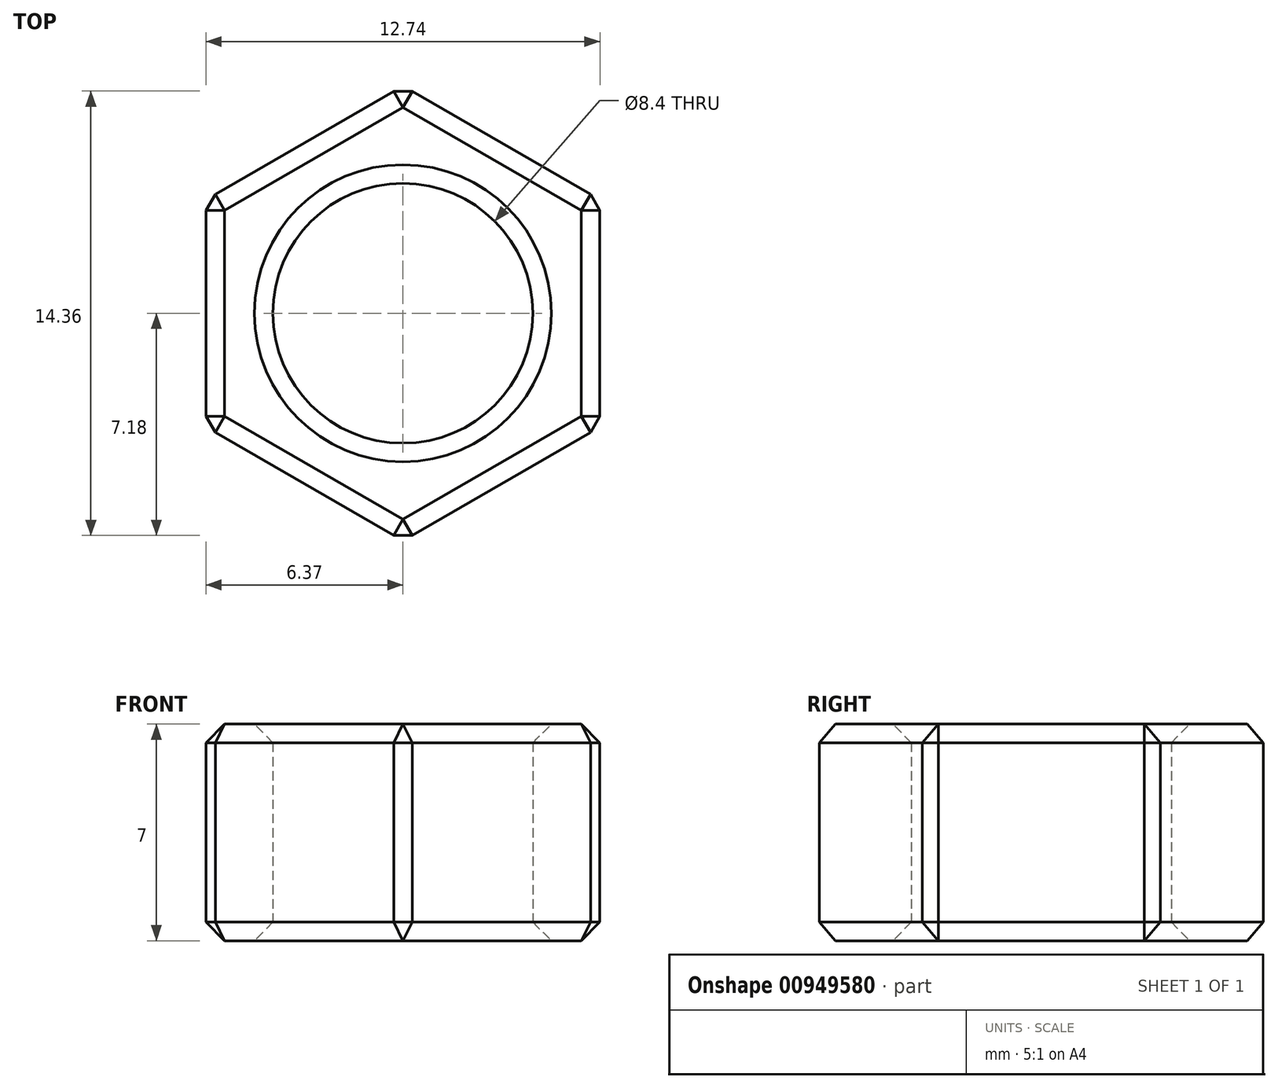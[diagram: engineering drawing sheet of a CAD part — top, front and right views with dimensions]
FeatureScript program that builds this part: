
annotation { "Feature Type Name" : "Feature", "Feature Type Description" : "" }
export const myFeature = defineFeature(function(context is Context, id is Id, definition is map)
    precondition{}
    {
        {
            var Q0;
            Q0=qCreatedBy(makeId("Top.planeOp"),FACE);
            var sketch = newSketch(context, id + "F0", { "sketchPlane" : qUnion([Q0])});
            skCircle(sketch, "E0.cCircle", {"center": v(0, 0) * mm, "radius": 7.35 * mm, "construction": true});
            skLineSegment(sketch, "E0.0", {"start": v(0, -7.35) * mm, "end": v(-6.37, -3.67) * mm});
            skLineSegment(sketch, "E0.1", {"start": v(-6.37, -3.68) * mm, "end": v(-6.37, 3.67) * mm});
            skLineSegment(sketch, "E0.2", {"start": v(-6.37, 3.67) * mm, "end": v(0, 7.35) * mm});
            skLineSegment(sketch, "E0.3", {"start": v(0, 7.35) * mm, "end": v(6.37, 3.68) * mm});
            skLineSegment(sketch, "E0.4", {"start": v(6.37, 3.68) * mm, "end": v(6.37, -3.67) * mm});
            skLineSegment(sketch, "E0.5", {"start": v(6.37, -3.67) * mm, "end": v(0, -7.35) * mm});
            skCircle(sketch, "E1", {"center": v(0, 0) * mm, "radius": 4.2 * mm});
            skSolve(sketch);
        }
        {
            var Q0;
            Q0=makeQuery(id+"F0.imprint","IMPRINT",FACE,{"disambiguationData":[TD([[makeQuery(id+"F0.imprint","IMPRINT",EDGE,{"derivedFrom":sQuery(id+"F0.wireOp",EDGE,"E0.0")}),-1.0]])]});
            extrude(context, id + "F1", {"entities" : qUnion([Q0]), "depth" : 7 * mm, "offsetDistance" : 25 * mm});
        }
        {
            var Q0;
            Q0=makeQuery(id+"F1.opExtrude","CAP_EDGE",EDGE,{"disambiguationData":[OSD([sQuery(id+"F0.wireOp",EDGE,"E0.4")])],"isStart":true});
            var Q1;
            Q1=makeQuery(id+"F1.opExtrude","CAP_EDGE",EDGE,{"disambiguationData":[OSD([sQuery(id+"F0.wireOp",EDGE,"E0.4")])],"isStart":false});
            var Q2;
            Q2=makeQuery(id+"F1.opExtrude","SWEPT_EDGE",EDGE,{"disambiguationData":[OSD([sQuery(id+"F0.wireOp",EDGE,"E0.0"),sQuery(id+"F0.wireOp",EDGE,"E0.5")])]});
            var Q3;
            Q3=makeQuery(id+"F1.opExtrude","SWEPT_EDGE",EDGE,{"disambiguationData":[OSD([sQuery(id+"F0.wireOp",EDGE,"E0.0"),sQuery(id+"F0.wireOp",EDGE,"E0.1")])]});
            var Q4;
            Q4=makeQuery(id+"F1.opExtrude","SWEPT_EDGE",EDGE,{"disambiguationData":[OSD([sQuery(id+"F0.wireOp",EDGE,"E0.3"),sQuery(id+"F0.wireOp",EDGE,"E0.4")])]});
            var Q5;
            Q5=makeQuery(id+"F1.opExtrude","SWEPT_EDGE",EDGE,{"disambiguationData":[OSD([sQuery(id+"F0.wireOp",EDGE,"E0.4"),sQuery(id+"F0.wireOp",EDGE,"E0.5")])]});
            var Q6;
            Q6=makeQuery(id+"F1.opExtrude","CAP_EDGE",EDGE,{"disambiguationData":[OSD([sQuery(id+"F0.wireOp",EDGE,"E0.1")])],"isStart":false});
            var Q7;
            Q7=makeQuery(id+"F1.opExtrude","CAP_EDGE",EDGE,{"disambiguationData":[OSD([sQuery(id+"F0.wireOp",EDGE,"E0.2")])],"isStart":false});
            var Q8;
            Q8=makeQuery(id+"F1.opExtrude","CAP_EDGE",EDGE,{"disambiguationData":[OSD([sQuery(id+"F0.wireOp",EDGE,"E0.5")])],"isStart":true});
            var Q9;
            Q9=makeQuery(id+"F1.opExtrude","CAP_EDGE",EDGE,{"disambiguationData":[OSD([sQuery(id+"F0.wireOp",EDGE,"E0.5")])],"isStart":false});
            var Q10;
            Q10=makeQuery(id+"F1.opExtrude","CAP_EDGE",EDGE,{"disambiguationData":[OSD([sQuery(id+"F0.wireOp",EDGE,"E1")])],"isStart":true});
            var Q11;
            Q11=makeQuery(id+"F1.opExtrude","CAP_EDGE",EDGE,{"disambiguationData":[OSD([sQuery(id+"F0.wireOp",EDGE,"E1")])],"isStart":false});
            var Q12;
            Q12=makeQuery(id+"F1.opExtrude","CAP_EDGE",EDGE,{"disambiguationData":[OSD([sQuery(id+"F0.wireOp",EDGE,"E0.3")])],"isStart":false});
            var Q13;
            Q13=makeQuery(id+"F1.opExtrude","SWEPT_EDGE",EDGE,{"disambiguationData":[OSD([sQuery(id+"F0.wireOp",EDGE,"E0.1"),sQuery(id+"F0.wireOp",EDGE,"E0.2")])]});
            var Q14;
            Q14=makeQuery(id+"F1.opExtrude","SWEPT_EDGE",EDGE,{"disambiguationData":[OSD([sQuery(id+"F0.wireOp",EDGE,"E0.2"),sQuery(id+"F0.wireOp",EDGE,"E0.3")])]});
            var Q15;
            Q15=makeQuery(id+"F1.opExtrude","CAP_EDGE",EDGE,{"disambiguationData":[OSD([sQuery(id+"F0.wireOp",EDGE,"E0.0")])],"isStart":true});
            var Q16;
            Q16=makeQuery(id+"F1.opExtrude","CAP_EDGE",EDGE,{"disambiguationData":[OSD([sQuery(id+"F0.wireOp",EDGE,"E0.0")])],"isStart":false});
            var Q17;
            Q17=makeQuery(id+"F1.opExtrude","CAP_EDGE",EDGE,{"disambiguationData":[OSD([sQuery(id+"F0.wireOp",EDGE,"E0.1")])],"isStart":true});
            var Q18;
            Q18=makeQuery(id+"F1.opExtrude","CAP_EDGE",EDGE,{"disambiguationData":[OSD([sQuery(id+"F0.wireOp",EDGE,"E0.2")])],"isStart":true});
            var Q19;
            Q19=makeQuery(id+"F1.opExtrude","CAP_EDGE",EDGE,{"disambiguationData":[OSD([sQuery(id+"F0.wireOp",EDGE,"E0.3")])],"isStart":true});
            chamfer(context, id + "F2", {"entities" : qUnion([Q0, Q1, Q2, Q3, Q4, Q5, Q6, Q7, Q8, Q9, Q10, Q11, Q12, Q13, Q14, Q15, Q16, Q17, Q18, Q19]), "width" : .6 * mm, "tangentPropagation" : true});
        }
    });
